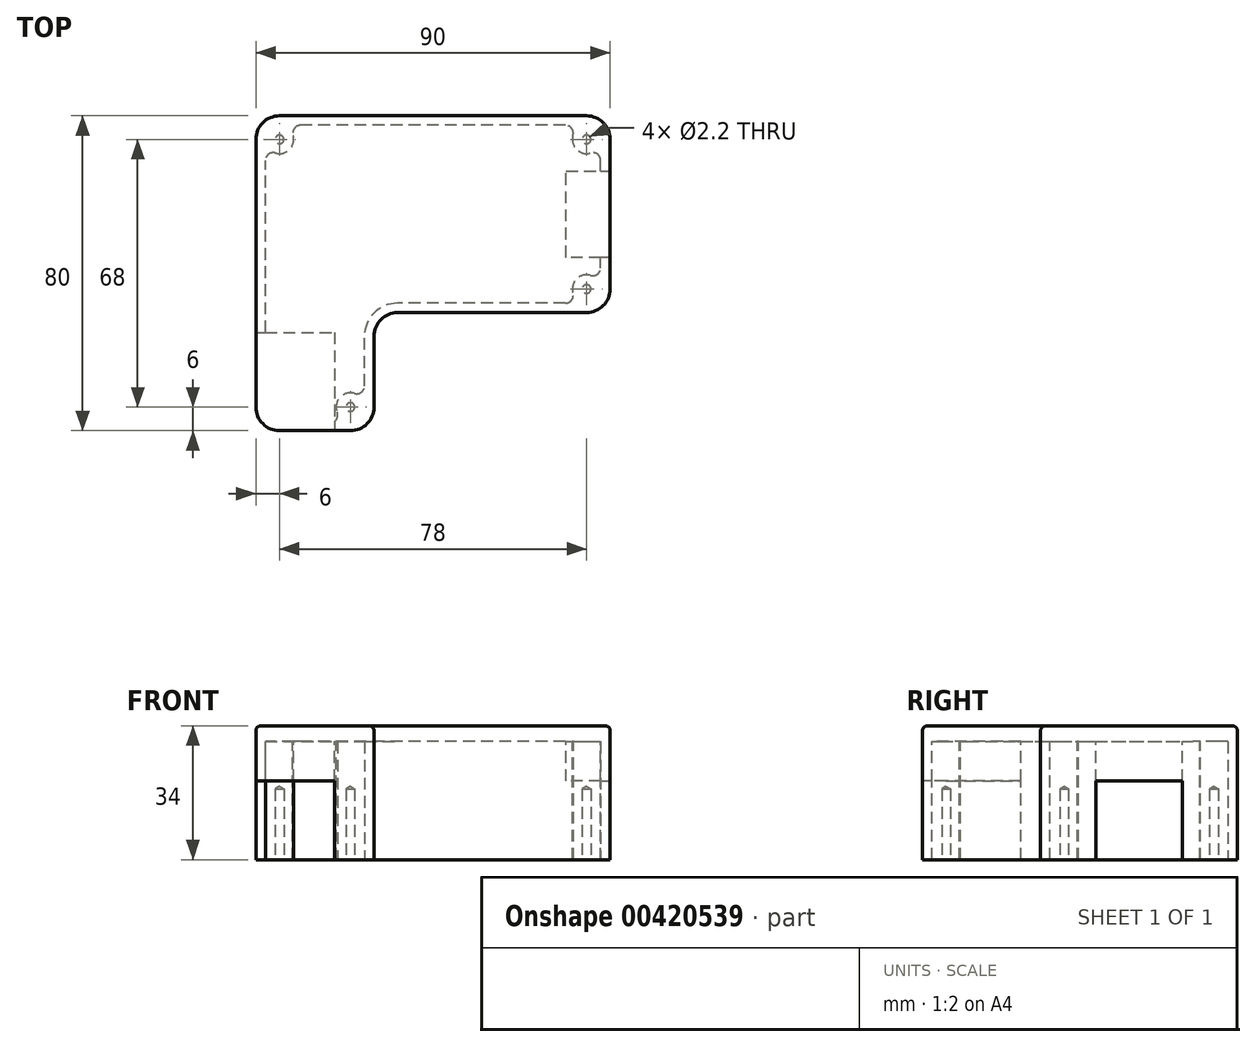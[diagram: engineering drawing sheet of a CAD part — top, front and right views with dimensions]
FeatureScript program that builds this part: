
annotation { "Feature Type Name" : "Feature", "Feature Type Description" : "" }
export const myFeature = defineFeature(function(context is Context, id is Id, definition is map)
    precondition{}
    {
        {
            var Q0;
            Q0=qCreatedBy(makeId("Top.planeOp"),FACE);
            var sketch = newSketch(context, id + "F0", { "sketchPlane" : qUnion([Q0])});
            skLineSegment(sketch, "E0.bottom", {"start": v(-15, -40) * mm, "end": v(-45, -40) * mm});
            skLineSegment(sketch, "E0.top", {"start": v(45, 40) * mm, "end": v(-45, 40) * mm});
            skLineSegment(sketch, "E0.left", {"start": v(45, -10) * mm, "end": v(45, 40) * mm});
            skLineSegment(sketch, "E0.right", {"start": v(-45, -40) * mm, "end": v(-45, 40) * mm});
            skPoint(sketch, "E0.middle", {"position": v(0, 0) * mm});
            skLineSegment(sketch, "E1.top", {"start": v(45, -10) * mm, "end": v(-15, -10) * mm});
            skLineSegment(sketch, "E1.right", {"start": v(-15, -40) * mm, "end": v(-15, -10) * mm});
            skPoint(sketch, "E2.orphan", {"position": v(45, -40) * mm});
            skSolve(sketch);
        }
        {
            var Q0;
            Q0=makeQuery(id+"F0.imprint","IMPRINT",FACE,{"disambiguationData":[TD([[makeQuery(id+"F0.imprint","IMPRINT",EDGE,{"derivedFrom":sQuery(id+"F0.wireOp",EDGE,"E0.bottom")}),-1.0]])]});
            extrude(context, id + "F1", {"entities" : qUnion([Q0]), "depth" : 4 * mm});
        }
        {
            var Q0;
            Q0=makeQuery(id+"F1.opExtrude","SWEPT_EDGE",EDGE,{"disambiguationData":[OSD([sQuery(id+"F0.wireOp",EDGE,"E0.bottom"),sQuery(id+"F0.wireOp",EDGE,"E1.right")])]});
            var Q1;
            Q1=makeQuery(id+"F1.opExtrude","SWEPT_EDGE",EDGE,{"disambiguationData":[OSD([sQuery(id+"F0.wireOp",EDGE,"E1.top"),sQuery(id+"F0.wireOp",EDGE,"E1.right")])]});
            var Q2;
            Q2=makeQuery(id+"F1.opExtrude","SWEPT_EDGE",EDGE,{"disambiguationData":[OSD([sQuery(id+"F0.wireOp",EDGE,"E0.left"),sQuery(id+"F0.wireOp",EDGE,"E1.top")])]});
            var Q3;
            Q3=makeQuery(id+"F1.opExtrude","SWEPT_EDGE",EDGE,{"disambiguationData":[OSD([sQuery(id+"F0.wireOp",EDGE,"E0.top"),sQuery(id+"F0.wireOp",EDGE,"E0.left")])]});
            var Q4;
            Q4=makeQuery(id+"F1.opExtrude","SWEPT_EDGE",EDGE,{"disambiguationData":[OSD([sQuery(id+"F0.wireOp",EDGE,"E0.top"),sQuery(id+"F0.wireOp",EDGE,"E0.right")])]});
            var Q5;
            Q5=makeQuery(id+"F1.opExtrude","SWEPT_EDGE",EDGE,{"disambiguationData":[OSD([sQuery(id+"F0.wireOp",EDGE,"E0.bottom"),sQuery(id+"F0.wireOp",EDGE,"E0.right")])]});
            fillet(context, id + "F2", {"entities" : qUnion([Q0, Q1, Q2, Q3, Q4, Q5]), "radius" : 6 * mm, "tangentPropagation" : true, "allowEdgeOverflow" : false});
        }
        {
            var Q0;
            Q0=makeQuery(id+"F1.opExtrude","CAP_FACE",FACE,{"disambiguationData":[OSD([sQuery(id+"F0.wireOp",EDGE,"E0.bottom"),sQuery(id+"F0.wireOp",EDGE,"E0.top"),sQuery(id+"F0.wireOp",EDGE,"E0.left"),sQuery(id+"F0.wireOp",EDGE,"E0.right"),sQuery(id+"F0.wireOp",EDGE,"E1.top"),sQuery(id+"F0.wireOp",EDGE,"E1.right")])],"isStart":true});
            var sketch = newSketch(context, id + "F3", { "sketchPlane" : qUnion([Q0])});
            skLineSegment(sketch, "E3", {"start": v(-45, 15) * mm, "end": v(-25, 15) * mm});
            skLineSegment(sketch, "E4", {"start": v(-25, 15) * mm, "end": v(-25, 40) * mm});
            skLineSegment(sketch, "E5", {"start": v(45, -4) * mm, "end": v(33.8, -4) * mm});
            skLineSegment(sketch, "E6", {"start": v(33.8, -4) * mm, "end": v(33.8, -26) * mm});
            skLineSegment(sketch, "E7", {"start": v(33.8, -26) * mm, "end": v(45, -26) * mm});
            skPoint(sketch, "E8", {"position": v(33.8, -15) * mm});
            skLineSegment(sketch, "E9", {"start": v(-25, 40) * mm, "end": v(-21, 40) * mm});
            skLineSegment(sketch, "E10", {"start": v(-45, 15) * mm, "end": v(-45, -34) * mm});
            skLineSegment(sketch, "E11", {"start": v(45, 4) * mm, "end": v(45, -4) * mm});
            skLineSegment(sketch, "E12", {"start": v(45, -26) * mm, "end": v(45, -34) * mm});
            skLineSegment(sketch, "E13.0", {"start": v(42.6, 4) * mm, "end": v(42.6, -4) * mm});
            skArc(sketch, "E13.1", {"start": v(42.6, 4) * mm, "mid": v(41.55, 6.55) * mm, "end": v(39, 7.6) * mm});
            skLineSegment(sketch, "E13.2", {"start": v(39, 7.6) * mm, "end": v(-9, 7.6) * mm});
            skLineSegment(sketch, "E13.3", {"start": v(-25, 37.6) * mm, "end": v(-21, 37.6) * mm});
            skArc(sketch, "E13.4", {"start": v(-17.4, 34) * mm, "mid": v(-18.45, 36.55) * mm, "end": v(-21, 37.6) * mm});
            skLineSegment(sketch, "E13.5", {"start": v(-17.4, 34) * mm, "end": v(-17.4, 16) * mm});
            skArc(sketch, "E13.6", {"start": v(-9, 7.6) * mm, "mid": v(-14.94, 10.06) * mm, "end": v(-17.4, 16) * mm});
            skLineSegment(sketch, "E14.0", {"start": v(42.6, -26) * mm, "end": v(42.6, -34) * mm});
            skLineSegment(sketch, "E14.1", {"start": v(-42.6, 15) * mm, "end": v(-42.6, -34) * mm});
            skArc(sketch, "E14.2", {"start": v(-42.6, -34) * mm, "mid": v(-41.55, -36.55) * mm, "end": v(-39, -37.6) * mm});
            skLineSegment(sketch, "E14.3", {"start": v(39, -37.6) * mm, "end": v(-39, -37.6) * mm});
            skArc(sketch, "E14.4", {"start": v(39, -37.6) * mm, "mid": v(41.55, -36.55) * mm, "end": v(42.6, -34) * mm});
            skCircle(sketch, "E15", {"center": v(-21, 34) * mm, "radius": 3.6 * mm});
            skCircle(sketch, "E16", {"center": v(-39, -34) * mm, "radius": 3.6 * mm});
            skCircle(sketch, "E17", {"center": v(39, -34) * mm, "radius": 3.6 * mm});
            skCircle(sketch, "E18", {"center": v(39, 4) * mm, "radius": 3.6 * mm});
            skLineSegment(sketch, "E19", {"start": v(-25, 40) * mm, "end": v(-39, 40) * mm});
            skLineSegment(sketch, "E20", {"start": v(-45, 15) * mm, "end": v(-45, 34) * mm});
            skLineSegment(sketch, "E21.0", {"start": v(-25, 37.6) * mm, "end": v(-39, 37.6) * mm});
            skArc(sketch, "E21.1", {"start": v(-39, 37.6) * mm, "mid": v(-41.55, 36.55) * mm, "end": v(-42.6, 34) * mm});
            skLineSegment(sketch, "E21.2", {"start": v(-42.6, 15) * mm, "end": v(-42.6, 34) * mm});
            skLineSegment(sketch, "E22", {"start": v(42.6, -4) * mm, "end": v(42.6, -26) * mm});
            skSolve(sketch);
        }
        {
            var Q0;
            {var subQ2=sQuery(id+"F3.wireOp",EDGE,"E9");Q0=makeQuery(id+"F3.imprint","IMPRINT",FACE,{"disambiguationData":[TD([[makeQuery(id+"F3.imprint","IMPRINT",EDGE,{"derivedFrom":subQ2}),1.0]])]});}
            var Q1;
            {var subQ5=sQuery(id+"F3.wireOp",EDGE,"E10");Q1=makeQuery(id+"F3.imprint","IMPRINT",FACE,{"disambiguationData":[TD([[makeQuery(id+"F3.imprint","IMPRINT",EDGE,{"derivedFrom":subQ5}),1.0]])]});}
            var Q2;
            {var subQ0=sQuery(id+"F3.wireOp",EDGE,"E18");var subQ1=makeQuery(id+"F3.imprint","INTERSECT",VERTEX,{"derivedFrom":[sQuery(id+"F3.wireOp",EDGE,"E13.0"),subQ0]});Q2=makeQuery(id+"F3.imprint","IMPRINT",FACE,{"disambiguationData":[TD([[makeQuery(id+"F3.imprint","IMPRINT",EDGE,{"disambiguationData":[TD([[subQ1,-1.0]])],"derivedFrom":subQ0}),1.0]])]});}
            var Q3;
            {var subQ0=sQuery(id+"F3.wireOp",EDGE,"E15");var subQ1=makeQuery(id+"F3.imprint","INTERSECT",VERTEX,{"derivedFrom":[sQuery(id+"F3.wireOp",EDGE,"E13.3"),subQ0]});Q3=makeQuery(id+"F3.imprint","IMPRINT",FACE,{"disambiguationData":[TD([[makeQuery(id+"F3.imprint","IMPRINT",EDGE,{"disambiguationData":[TD([[subQ1,1.0]])],"derivedFrom":subQ0}),1.0]])]});}
            var Q4;
            {var subQ0=sQuery(id+"F3.wireOp",EDGE,"E16");var subQ1=makeQuery(id+"F3.imprint","INTERSECT",VERTEX,{"derivedFrom":[sQuery(id+"F3.wireOp",EDGE,"E14.1"),subQ0]});Q4=makeQuery(id+"F3.imprint","IMPRINT",FACE,{"disambiguationData":[TD([[makeQuery(id+"F3.imprint","IMPRINT",EDGE,{"disambiguationData":[TD([[subQ1,-1.0]])],"derivedFrom":subQ0}),1.0]])]});}
            var Q5;
            {var subQ0=sQuery(id+"F3.wireOp",EDGE,"E17");var subQ1=makeQuery(id+"F3.imprint","INTERSECT",VERTEX,{"derivedFrom":[sQuery(id+"F3.wireOp",EDGE,"E14.0"),subQ0]});Q5=makeQuery(id+"F3.imprint","IMPRINT",FACE,{"disambiguationData":[TD([[makeQuery(id+"F3.imprint","IMPRINT",EDGE,{"disambiguationData":[TD([[subQ1,-1.0]])],"derivedFrom":subQ0}),1.0]])]});}
            extrude(context, id + "F4", {"entities" : qUnion([Q0, Q1, Q2, Q3, Q4, Q5]), "operationType" : NewBodyOperationType.ADD, "depth" : 30 * mm});
        }
        {
            var Q0;
            Q0=makeQuery(id+"F4.opExtrude","SWEPT_EDGE",EDGE,{"disambiguationData":[OSD([sQuery(id+"F3.wireOp",EDGE,"E13.0"),sQuery(id+"F3.wireOp",EDGE,"E18")])]});
            var Q1;
            Q1=makeQuery(id+"F4.opExtrude","SWEPT_EDGE",EDGE,{"disambiguationData":[OSD([sQuery(id+"F3.wireOp",EDGE,"E13.2"),sQuery(id+"F3.wireOp",EDGE,"E18")])]});
            var Q2;
            Q2=makeQuery(id+"F4.opExtrude","SWEPT_EDGE",EDGE,{"disambiguationData":[OSD([sQuery(id+"F3.wireOp",EDGE,"E13.3"),sQuery(id+"F3.wireOp",EDGE,"E15")])]});
            var Q3;
            Q3=makeQuery(id+"F4.opExtrude","SWEPT_EDGE",EDGE,{"disambiguationData":[OSD([sQuery(id+"F3.wireOp",EDGE,"E13.5"),sQuery(id+"F3.wireOp",EDGE,"E15")])]});
            var Q4;
            Q4=makeQuery(id+"F4.opExtrude","SWEPT_EDGE",EDGE,{"disambiguationData":[OSD([sQuery(id+"F3.wireOp",EDGE,"E14.1"),sQuery(id+"F3.wireOp",EDGE,"E16")])]});
            var Q5;
            Q5=makeQuery(id+"F4.opExtrude","SWEPT_EDGE",EDGE,{"disambiguationData":[OSD([sQuery(id+"F3.wireOp",EDGE,"E14.3"),sQuery(id+"F3.wireOp",EDGE,"E16")])]});
            var Q6;
            Q6=makeQuery(id+"F4.opExtrude","SWEPT_EDGE",EDGE,{"disambiguationData":[OSD([sQuery(id+"F3.wireOp",EDGE,"E14.0"),sQuery(id+"F3.wireOp",EDGE,"E17")])]});
            var Q7;
            Q7=makeQuery(id+"F4.opExtrude","SWEPT_EDGE",EDGE,{"disambiguationData":[OSD([sQuery(id+"F3.wireOp",EDGE,"E14.3"),sQuery(id+"F3.wireOp",EDGE,"E17")])]});
            fillet(context, id + "F5", {"entities" : qUnion([Q0, Q1, Q2, Q3, Q4, Q5, Q6, Q7]), "radius" : 2 * mm, "tangentPropagation" : true, "allowEdgeOverflow" : false});
        }
        {
            var Q0;
            {var subQ3=sQuery(id+"F3.wireOp",EDGE,"E22");Q0=makeQuery(id+"F3.imprint","IMPRINT",FACE,{"disambiguationData":[TD([[makeQuery(id+"F3.imprint","IMPRINT",EDGE,{"derivedFrom":subQ3}),1.0]])]});}
            var Q1;
            {var subQ0=sQuery(id+"F3.wireOp",EDGE,"E19");Q1=makeQuery(id+"F3.imprint","IMPRINT",FACE,{"disambiguationData":[TD([[makeQuery(id+"F3.imprint","IMPRINT",EDGE,{"derivedFrom":subQ0}),1.0]])]});}
            var Q2;
            {var subQ3=sQuery(id+"F3.wireOp",EDGE,"E21.0");Q2=makeQuery(id+"F3.imprint","IMPRINT",FACE,{"disambiguationData":[TD([[makeQuery(id+"F3.imprint","IMPRINT",EDGE,{"derivedFrom":subQ3}),1.0]])]});}
            var Q3;
            {var subQ0=sQuery(id+"F3.wireOp",EDGE,"E6");Q3=makeQuery(id+"F3.imprint","IMPRINT",FACE,{"disambiguationData":[TD([[makeQuery(id+"F3.imprint","IMPRINT",EDGE,{"derivedFrom":subQ0}),1.0]])]});}
            extrude(context, id + "F6", {"entities" : qUnion([Q0, Q1, Q2, Q3]), "operationType" : NewBodyOperationType.ADD, "depth" : 10 * mm});
        }
        {
            var Q0;
            Q0=makeQuery(id+"F4.opExtrude","CAP_FACE",FACE,{"disambiguationData":[OSD([sQuery(id+"F0.wireOp",EDGE,"E0.bottom"),sQuery(id+"F0.wireOp",EDGE,"E0.top"),sQuery(id+"F0.wireOp",EDGE,"E0.left"),sQuery(id+"F0.wireOp",EDGE,"E0.right"),sQuery(id+"F0.wireOp",EDGE,"E1.top"),sQuery(id+"F0.wireOp",EDGE,"E1.right"),sQuery(id+"F3.wireOp",EDGE,"E4"),sQuery(id+"F3.wireOp",EDGE,"E5"),sQuery(id+"F3.wireOp",EDGE,"E9"),sQuery(id+"F3.wireOp",EDGE,"E11"),sQuery(id+"F3.wireOp",EDGE,"E13.0"),sQuery(id+"F3.wireOp",EDGE,"E13.2"),sQuery(id+"F3.wireOp",EDGE,"E13.3"),sQuery(id+"F3.wireOp",EDGE,"E13.5"),sQuery(id+"F3.wireOp",EDGE,"E13.6"),sQuery(id+"F3.wireOp",EDGE,"E15"),sQuery(id+"F3.wireOp",EDGE,"E18")])],"isStart":false});
            var sketch = newSketch(context, id + "F7", { "sketchPlane" : qUnion([Q0])});
            skPoint(sketch, "E23", {"position": v(-21, 34) * mm});
            skPoint(sketch, "E24", {"position": v(39, 4) * mm});
            skSolve(sketch);
        }
        {
            var Q0;
            Q0=makeQuery(id+"F4.opExtrude","CAP_FACE",FACE,{"disambiguationData":[OSD([sQuery(id+"F0.wireOp",EDGE,"E0.bottom"),sQuery(id+"F0.wireOp",EDGE,"E0.top"),sQuery(id+"F0.wireOp",EDGE,"E0.left"),sQuery(id+"F0.wireOp",EDGE,"E0.right"),sQuery(id+"F0.wireOp",EDGE,"E1.top"),sQuery(id+"F0.wireOp",EDGE,"E1.right"),sQuery(id+"F3.wireOp",EDGE,"E3"),sQuery(id+"F3.wireOp",EDGE,"E7"),sQuery(id+"F3.wireOp",EDGE,"E10"),sQuery(id+"F3.wireOp",EDGE,"E12"),sQuery(id+"F3.wireOp",EDGE,"E14.0"),sQuery(id+"F3.wireOp",EDGE,"E14.1"),sQuery(id+"F3.wireOp",EDGE,"E14.3"),sQuery(id+"F3.wireOp",EDGE,"E16"),sQuery(id+"F3.wireOp",EDGE,"E17")])],"isStart":false});
            var sketch = newSketch(context, id + "F8", { "sketchPlane" : qUnion([Q0])});
            skPoint(sketch, "E25", {"position": v(-39, -34) * mm});
            skPoint(sketch, "E26", {"position": v(39, -34) * mm});
            skSolve(sketch);
        }
        {
            var Q0;
            Q0=sQuery(id+"F7.wireOp",VERTEX,"E23");
            var Q1;
            Q1=sQuery(id+"F8.wireOp",VERTEX,"E25");
            var Q2;
            Q2=sQuery(id+"F7.wireOp",VERTEX,"E24");
            var Q3;
            Q3=sQuery(id+"F8.wireOp",VERTEX,"E26");
            var Q4;
            Q4=makeQuery(id+"F1.opExtrude","SWEPT_BODY",BODY,{"disambiguationData":[OSD([sQuery(id+"F0.wireOp",EDGE,"E0.bottom"),sQuery(id+"F0.wireOp",EDGE,"E0.top"),sQuery(id+"F0.wireOp",EDGE,"E0.left"),sQuery(id+"F0.wireOp",EDGE,"E0.right"),sQuery(id+"F0.wireOp",EDGE,"E1.top"),sQuery(id+"F0.wireOp",EDGE,"E1.right")])]});
            hole(context, id + "F9", {"style" : HoleStyle.SIMPLE, "endStyle" : HoleEndStyle.BLIND, "holeDiameter" : 2.2 * mm, "holeDepth" : 18 * mm, "isTappedThrough" : true, "tappedDepth" : 12 * mm, "tapClearance" : 3, "locations" : qUnion([Q0, Q1, Q2, Q3]), "scope" : qUnion([Q4])});
        }
        {
            var Q0;
            Q0=makeQuery(id+"F1.opExtrude","CAP_FACE",FACE,{"disambiguationData":[OSD([sQuery(id+"F0.wireOp",EDGE,"E0.bottom"),sQuery(id+"F0.wireOp",EDGE,"E0.top"),sQuery(id+"F0.wireOp",EDGE,"E0.left"),sQuery(id+"F0.wireOp",EDGE,"E0.right"),sQuery(id+"F0.wireOp",EDGE,"E1.top"),sQuery(id+"F0.wireOp",EDGE,"E1.right")])],"isStart":false});
            fillet(context, id + "F10", {"entities" : qUnion([Q0]), "radius" : 1.2 * mm, "tangentPropagation" : true, "allowEdgeOverflow" : false});
        }
    });
